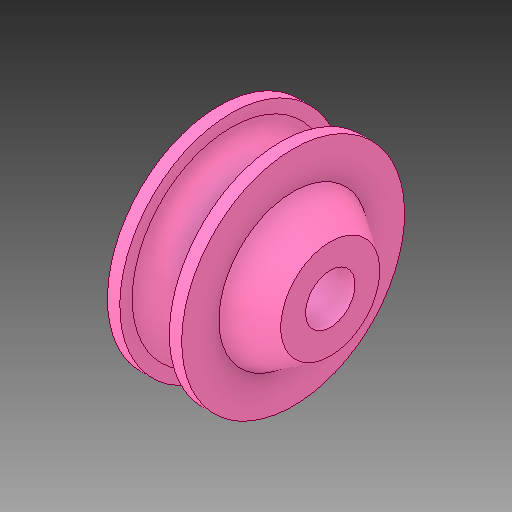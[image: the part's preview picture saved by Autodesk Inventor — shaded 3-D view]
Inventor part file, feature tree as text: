
AUTODESK INVENTOR PART (.ipt)
format: ipt  version: 2017 SP1 (Build 210196100, 196)  size: 197,120 bytes
history: native  units: in
note: dims shown in document units (in); Inventor stores cm internally (conversion verified against a paired STEP export)
features: sketch x2, revolve x1, extrude x1
ambient origin geometry x8: Origin, YZ Plane, XZ Plane, XY Plane, X Axis, Y Axis, Z Axis, Center Point
bodies: Solid1 (feature_tree)
feature tree (4):
  revolve  "Revolution1"  [1 undecoded]
  extrude  "Extrusion1"  Depth=0.125in
  sketch  "Sketch1"  dims[d1=0.0625in d2=0.0625in]
  sketch  "Sketch2"  dims[d7=0.375in d8=0.125in d10=0.125in d11=0.375in d12=0.75in d13=0.125in d14=0.125in d15=90.0deg d16=0.625in d17=0.25in d18=0.0in]
note: 1 required parameter value undecoded (feature->parameter linkage not recoverable at this tier; creation-order binding heuristic only, values carry confidence <= 0.55)
